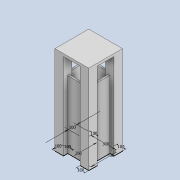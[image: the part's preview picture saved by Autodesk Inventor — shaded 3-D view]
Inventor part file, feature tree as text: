
AUTODESK INVENTOR PART (.ipt)
format: ipt  version: 2021 (Build 250183000, 183)  size: 142,336 bytes
history: native  units: mm
features: extrude x4, sketch x2
ambient origin geometry x8: Origin, YZ Plane, XZ Plane, XY Plane, X Axis, Y Axis, Z Axis, Center Point
bodies: Solid1 (feature_tree)
feature tree (6):
  sketch  "Sketch1"  dims[d0=300.0mm d1=300.0mm]
  extrude  "Extrusion1"  Depth=300.0mm
  extrude  "Extrusion2"  Depth=100.0mm
  extrude  "Extrusion3"  Depth=100.0mm
  extrude  "Extrusion4"  Depth=100.0mm
  sketch  "Sketch2"  dims[d2=100.0mm d3=100.0mm d4=100.0mm d5=100.0mm d6=100.0mm d7=100.0mm d8=1050.0mm d9=0.0mm d10=800.0mm d11=0.0mm d12=30.0mm d13=0.0mm d14=260.0mm d15=10.0mm d16=0.0mm]
